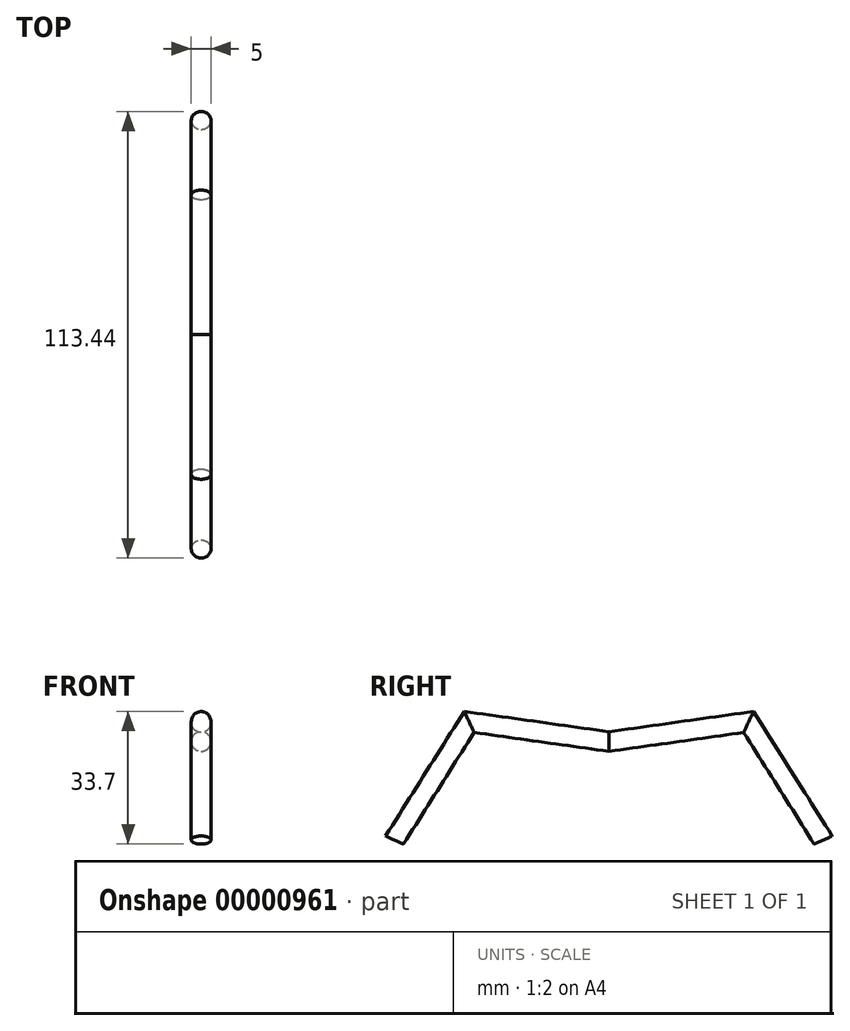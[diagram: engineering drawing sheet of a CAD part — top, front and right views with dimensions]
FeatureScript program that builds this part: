
annotation { "Feature Type Name" : "Feature", "Feature Type Description" : "" }
export const myFeature = defineFeature(function(context is Context, id is Id, definition is map)
    precondition{}
    {
        {
            var Q0;
            Q0=qCreatedBy(makeId("Front.planeOp"),FACE);
            var sketch = newSketch(context, id + "F0", { "sketchPlane" : qUnion([Q0])});
            skCircle(sketch, "E0", {"center": v(0, 0) * mm, "radius": 2.5 * mm});
            skSolve(sketch);
        }
        {
            var Q0;
            Q0=qCreatedBy(makeId("Right.planeOp"),FACE);
            var sketch = newSketch(context, id + "F1", { "sketchPlane" : qUnion([Q0])});
            skLineSegment(sketch, "E1", {"start": v(0, 0) * mm, "end": v(-35.49, 4.98) * mm});
            skLineSegment(sketch, "E2", {"start": v(-35.49, 4.98) * mm, "end": v(-54.44, -25.02) * mm});
            skSolve(sketch);
        }
        {
            var Q0;
            Q0=makeQuery(id+"F0.imprint","IMPRINT",FACE,{"disambiguationData":[TD([[makeQuery(id+"F0.imprint","IMPRINT",EDGE,{"derivedFrom":sQuery(id+"F0.wireOp",EDGE,"E0")}),1.0]])]});
            var Q1;
            Q1=sQuery(id+"F1.wireOp",EDGE,"E1");
            var Q2;
            Q2=sQuery(id+"F1.wireOp",EDGE,"E2");
            sweep(context, id + "F2", {"profiles" : qUnion([Q0]), "path" : qUnion([Q1, Q2])});
        }
        {
            var Q0;
            Q0=makeQuery(id+"F2.opSweep","SWEPT_BODY",BODY,{"disambiguationData":[OSD([sQuery(id+"F0.wireOp",EDGE,"E0"),sQuery(id+"F1.wireOp",EDGE,"E2")])]});
            var Q1;
            Q1=qCreatedBy(makeId("Front.planeOp"),FACE);
            mirror(context, id + "F3", {"entities" : qUnion([Q0]), "mirrorPlane" : qUnion([Q1])});
        }
    });
